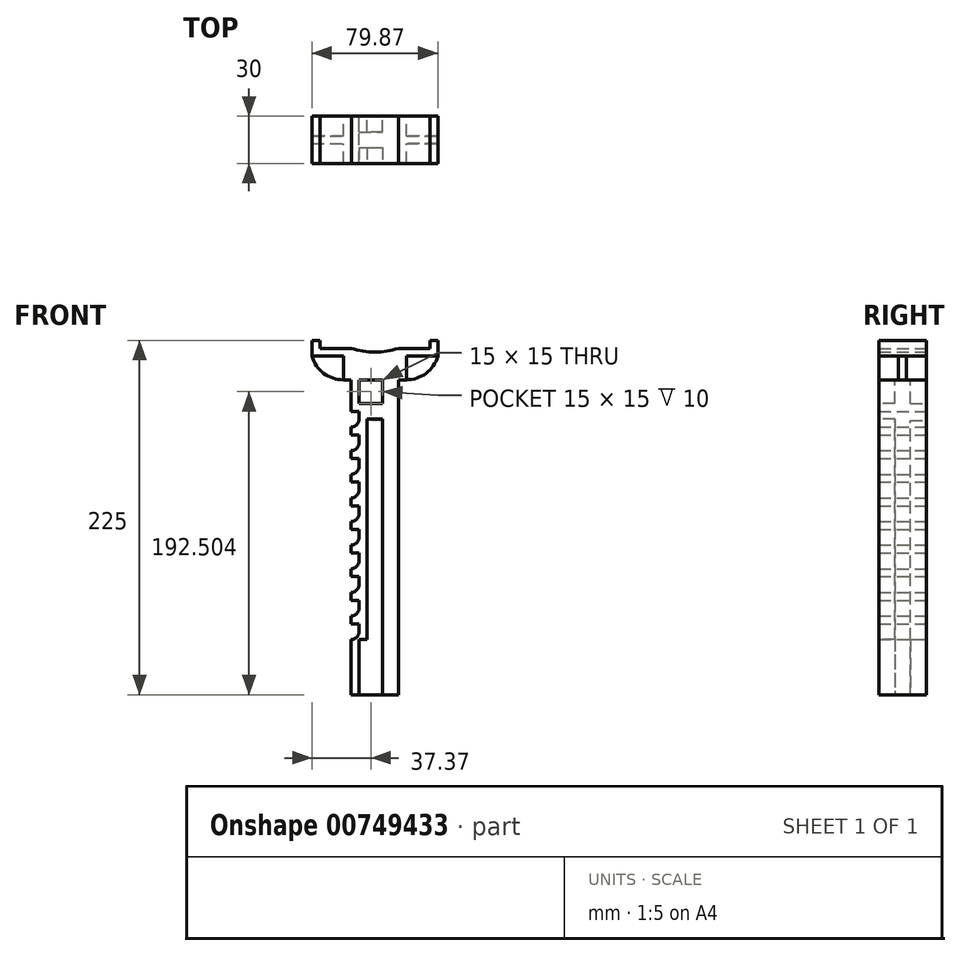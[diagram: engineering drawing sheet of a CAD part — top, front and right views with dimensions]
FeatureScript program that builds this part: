
annotation { "Feature Type Name" : "Feature", "Feature Type Description" : "" }
export const myFeature = defineFeature(function(context is Context, id is Id, definition is map)
    precondition{}
    {
        {
            var Q0;
            Q0=qCreatedBy(makeId("Front.planeOp"),FACE);
            var sketch = newSketch(context, id + "F0", { "sketchPlane" : qUnion([Q0])});
            skLineSegment(sketch, "E0.top", {"start": v(-25, -77.98) * mm, "end": v(5, -77.98) * mm});
            skLineSegment(sketch, "E0.left", {"start": v(-25, 122.02) * mm, "end": v(-25, 102.02) * mm});
            skLineSegment(sketch, "E0.right", {"start": v(5, 122.02) * mm, "end": v(5, -77.98) * mm});
            skLineSegment(sketch, "E1.bottom", {"start": v(-30, 122.02) * mm, "end": v(-25, 122.02) * mm});
            skLineSegment(sketch, "E1.top", {"start": v(-30, 137.02) * mm, "end": v(10, 137.02) * mm});
            skLineSegment(sketch, "E1.left", {"start": v(-30, 122.02) * mm, "end": v(-30, 137.02) * mm});
            skLineSegment(sketch, "E1.right", {"start": v(10, 122.02) * mm, "end": v(10, 137.02) * mm});
            skLineSegment(sketch, "E2", {"start": v(-20, -42.98) * mm, "end": v(-20, -32.98) * mm});
            skPoint(sketch, "E3.start.orphan", {"position": v(-25, 102.02) * mm});
            skPoint(sketch, "E4.start.orphan", {"position": v(-25, -42.98) * mm});
            skLineSegment(sketch, "E5.trimOffspring", {"start": v(-25, -42.98) * mm, "end": v(-25, -77.98) * mm});
            skLineSegment(sketch, "E6", {"start": v(-25, -42.98) * mm, "end": v(-20, -42.98) * mm});
            skLineSegment(sketch, "E7", {"start": v(-25, 102.02) * mm, "end": v(-20, 102.02) * mm});
            skPoint(sketch, "E8.orphan", {"position": v(-20, -77.98) * mm});
            skLineSegment(sketch, "E9.trimOffspring", {"start": v(5, 122.02) * mm, "end": v(10, 122.02) * mm});
            skLineSegment(sketch, "E10.bottom", {"start": v(-20, 92.02) * mm, "end": v(-25, 92.02) * mm});
            skLineSegment(sketch, "E10.top", {"start": v(-20, 87.02) * mm, "end": v(-25, 87.02) * mm});
            skLineSegment(sketch, "E10.right", {"start": v(-25, 92.02) * mm, "end": v(-25, 87.02) * mm});
            skLineSegment(sketch, "E11.bottom", {"start": v(-20, 77.02) * mm, "end": v(-25, 77.02) * mm});
            skLineSegment(sketch, "E11.top", {"start": v(-20, 72.02) * mm, "end": v(-25, 72.02) * mm});
            skLineSegment(sketch, "E11.right", {"start": v(-25, 77.02) * mm, "end": v(-25, 72.02) * mm});
            skLineSegment(sketch, "E12.bottom", {"start": v(-20, 62.02) * mm, "end": v(-25, 62.02) * mm});
            skLineSegment(sketch, "E12.top", {"start": v(-20, 57.02) * mm, "end": v(-25, 57.02) * mm});
            skLineSegment(sketch, "E12.right", {"start": v(-25, 62.02) * mm, "end": v(-25, 57.02) * mm});
            skLineSegment(sketch, "E13.bottom", {"start": v(-20, 47.02) * mm, "end": v(-25, 47.02) * mm});
            skLineSegment(sketch, "E13.top", {"start": v(-20, 42.02) * mm, "end": v(-25, 42.02) * mm});
            skLineSegment(sketch, "E13.right", {"start": v(-25, 47.02) * mm, "end": v(-25, 42.02) * mm});
            skLineSegment(sketch, "E14.bottom", {"start": v(-20, 32.02) * mm, "end": v(-25, 32.02) * mm});
            skLineSegment(sketch, "E14.top", {"start": v(-20, 27.02) * mm, "end": v(-25, 27.02) * mm});
            skLineSegment(sketch, "E14.right", {"start": v(-25, 32.02) * mm, "end": v(-25, 27.02) * mm});
            skLineSegment(sketch, "E15.bottom", {"start": v(-20, 17.02) * mm, "end": v(-25, 17.02) * mm});
            skLineSegment(sketch, "E15.top", {"start": v(-20, 12.02) * mm, "end": v(-25, 12.02) * mm});
            skLineSegment(sketch, "E15.right", {"start": v(-25, 17.02) * mm, "end": v(-25, 12.02) * mm});
            skLineSegment(sketch, "E16.bottom", {"start": v(-20, 2.02) * mm, "end": v(-25, 2.02) * mm});
            skLineSegment(sketch, "E16.top", {"start": v(-20, -2.98) * mm, "end": v(-25, -2.98) * mm});
            skLineSegment(sketch, "E16.right", {"start": v(-25, 2.02) * mm, "end": v(-25, -2.98) * mm});
            skLineSegment(sketch, "E17.bottom", {"start": v(-20, -12.98) * mm, "end": v(-25, -12.98) * mm});
            skLineSegment(sketch, "E17.top", {"start": v(-20, -17.98) * mm, "end": v(-25, -17.98) * mm});
            skLineSegment(sketch, "E17.right", {"start": v(-25, -12.98) * mm, "end": v(-25, -17.98) * mm});
            skLineSegment(sketch, "E18.bottom", {"start": v(-20, -27.98) * mm, "end": v(-25, -27.98) * mm});
            skLineSegment(sketch, "E18.top", {"start": v(-20, -32.98) * mm, "end": v(-25, -32.98) * mm});
            skLineSegment(sketch, "E18.right", {"start": v(-25, -27.98) * mm, "end": v(-25, -32.98) * mm});
            skLineSegment(sketch, "E19.trimOffspring", {"start": v(-20, 92.02) * mm, "end": v(-20, 102.02) * mm});
            skLineSegment(sketch, "E20.trimOffspring", {"start": v(-20, 77.02) * mm, "end": v(-20, 87.02) * mm});
            skLineSegment(sketch, "E21.trimOffspring", {"start": v(-20, 62.02) * mm, "end": v(-20, 72.02) * mm});
            skLineSegment(sketch, "E22.trimOffspring", {"start": v(-20, 47.02) * mm, "end": v(-20, 57.02) * mm});
            skLineSegment(sketch, "E23.trimOffspring", {"start": v(-20, 32.02) * mm, "end": v(-20, 42.02) * mm});
            skLineSegment(sketch, "E24.trimOffspring", {"start": v(-20, 17.02) * mm, "end": v(-20, 27.02) * mm});
            skLineSegment(sketch, "E25.trimOffspring", {"start": v(-20, 2.02) * mm, "end": v(-20, 12.02) * mm});
            skLineSegment(sketch, "E26.trimOffspring", {"start": v(-20, -12.98) * mm, "end": v(-20, -2.98) * mm});
            skLineSegment(sketch, "E27.trimOffspring", {"start": v(-20, -27.98) * mm, "end": v(-20, -17.98) * mm});
            skSolve(sketch);
        }
        {
            var Q0;
            Q0 = qSketchRegion(id + "F0", true);
            extrude(context, id + "F1", {"entities" : qUnion([Q0]), "depth" : 30 * mm, "offsetDistance" : 25 * mm});
        }
        {
            var Q0;
            Q0=makeQuery(id+"F1.opExtrude","SWEPT_EDGE",EDGE,{"disambiguationData":[OSD([sQuery(id+"F0.wireOp",EDGE,"E10.bottom"),sQuery(id+"F0.wireOp",EDGE,"E19.trimOffspring")])]});
            var Q1;
            Q1=makeQuery(id+"F1.opExtrude","SWEPT_EDGE",EDGE,{"disambiguationData":[OSD([sQuery(id+"F0.wireOp",EDGE,"E11.bottom"),sQuery(id+"F0.wireOp",EDGE,"E20.trimOffspring")])]});
            var Q2;
            Q2=makeQuery(id+"F1.opExtrude","SWEPT_EDGE",EDGE,{"disambiguationData":[OSD([sQuery(id+"F0.wireOp",EDGE,"E12.bottom"),sQuery(id+"F0.wireOp",EDGE,"E21.trimOffspring")])]});
            var Q3;
            Q3=makeQuery(id+"F1.opExtrude","SWEPT_EDGE",EDGE,{"disambiguationData":[OSD([sQuery(id+"F0.wireOp",EDGE,"E13.bottom"),sQuery(id+"F0.wireOp",EDGE,"E22.trimOffspring")])]});
            var Q4;
            Q4=makeQuery(id+"F1.opExtrude","SWEPT_EDGE",EDGE,{"disambiguationData":[OSD([sQuery(id+"F0.wireOp",EDGE,"E14.bottom"),sQuery(id+"F0.wireOp",EDGE,"E23.trimOffspring")])]});
            var Q5;
            Q5=makeQuery(id+"F1.opExtrude","SWEPT_EDGE",EDGE,{"disambiguationData":[OSD([sQuery(id+"F0.wireOp",EDGE,"E15.bottom"),sQuery(id+"F0.wireOp",EDGE,"E24.trimOffspring")])]});
            var Q6;
            Q6=makeQuery(id+"F1.opExtrude","SWEPT_EDGE",EDGE,{"disambiguationData":[OSD([sQuery(id+"F0.wireOp",EDGE,"E16.bottom"),sQuery(id+"F0.wireOp",EDGE,"E25.trimOffspring")])]});
            var Q7;
            Q7=makeQuery(id+"F1.opExtrude","SWEPT_EDGE",EDGE,{"disambiguationData":[OSD([sQuery(id+"F0.wireOp",EDGE,"E17.bottom"),sQuery(id+"F0.wireOp",EDGE,"E26.trimOffspring")])]});
            var Q8;
            Q8=makeQuery(id+"F1.opExtrude","SWEPT_EDGE",EDGE,{"disambiguationData":[OSD([sQuery(id+"F0.wireOp",EDGE,"E18.bottom"),sQuery(id+"F0.wireOp",EDGE,"E27.trimOffspring")])]});
            var Q9;
            Q9=makeQuery(id+"F1.opExtrude","SWEPT_EDGE",EDGE,{"disambiguationData":[OSD([sQuery(id+"F0.wireOp",EDGE,"E2"),sQuery(id+"F0.wireOp",EDGE,"E6")])]});
            fillet(context, id + "F2", {"entities" : qUnion([Q0, Q1, Q2, Q3, Q4, Q5, Q6, Q7, Q8, Q9]), "radius" : 5 * mm, "tangentPropagation" : true, "allowEdgeOverflow" : false});
        }
        {
            var Q0;
            Q0=makeQuery(id+"F1.opExtrude","CAP_FACE",FACE,{"disambiguationData":[OSD([sQuery(id+"F0.wireOp",EDGE,"E0.top"),sQuery(id+"F0.wireOp",EDGE,"E0.left"),sQuery(id+"F0.wireOp",EDGE,"E0.right"),sQuery(id+"F0.wireOp",EDGE,"E1.bottom"),sQuery(id+"F0.wireOp",EDGE,"E1.top"),sQuery(id+"F0.wireOp",EDGE,"E1.left"),sQuery(id+"F0.wireOp",EDGE,"E1.right"),sQuery(id+"F0.wireOp",EDGE,"E2"),sQuery(id+"F0.wireOp",EDGE,"E5.trimOffspring"),sQuery(id+"F0.wireOp",EDGE,"E6"),sQuery(id+"F0.wireOp",EDGE,"E7"),sQuery(id+"F0.wireOp",EDGE,"E9.trimOffspring"),sQuery(id+"F0.wireOp",EDGE,"E10.bottom"),sQuery(id+"F0.wireOp",EDGE,"E10.top"),sQuery(id+"F0.wireOp",EDGE,"E10.right"),sQuery(id+"F0.wireOp",EDGE,"E11.bottom"),sQuery(id+"F0.wireOp",EDGE,"E11.top"),sQuery(id+"F0.wireOp",EDGE,"E11.right"),sQuery(id+"F0.wireOp",EDGE,"E12.bottom"),sQuery(id+"F0.wireOp",EDGE,"E12.top"),sQuery(id+"F0.wireOp",EDGE,"E12.right"),sQuery(id+"F0.wireOp",EDGE,"E13.bottom"),sQuery(id+"F0.wireOp",EDGE,"E13.top"),sQuery(id+"F0.wireOp",EDGE,"E13.right"),sQuery(id+"F0.wireOp",EDGE,"E14.bottom"),sQuery(id+"F0.wireOp",EDGE,"E14.top"),sQuery(id+"F0.wireOp",EDGE,"E14.right"),sQuery(id+"F0.wireOp",EDGE,"E15.bottom"),sQuery(id+"F0.wireOp",EDGE,"E15.top"),sQuery(id+"F0.wireOp",EDGE,"E15.right"),sQuery(id+"F0.wireOp",EDGE,"E16.bottom"),sQuery(id+"F0.wireOp",EDGE,"E16.top"),sQuery(id+"F0.wireOp",EDGE,"E16.right"),sQuery(id+"F0.wireOp",EDGE,"E17.bottom"),sQuery(id+"F0.wireOp",EDGE,"E17.top"),sQuery(id+"F0.wireOp",EDGE,"E17.right"),sQuery(id+"F0.wireOp",EDGE,"E18.bottom"),sQuery(id+"F0.wireOp",EDGE,"E18.top"),sQuery(id+"F0.wireOp",EDGE,"E18.right"),sQuery(id+"F0.wireOp",EDGE,"E19.trimOffspring"),sQuery(id+"F0.wireOp",EDGE,"E20.trimOffspring"),sQuery(id+"F0.wireOp",EDGE,"E21.trimOffspring"),sQuery(id+"F0.wireOp",EDGE,"E22.trimOffspring"),sQuery(id+"F0.wireOp",EDGE,"E23.trimOffspring"),sQuery(id+"F0.wireOp",EDGE,"E24.trimOffspring"),sQuery(id+"F0.wireOp",EDGE,"E25.trimOffspring"),sQuery(id+"F0.wireOp",EDGE,"E26.trimOffspring"),sQuery(id+"F0.wireOp",EDGE,"E27.trimOffspring")])],"isStart":false});
            var sketch = newSketch(context, id + "F3", { "sketchPlane" : qUnion([Q0])});
            skLineSegment(sketch, "E28", {"start": v(-20, -42.98) * mm, "end": v(-20, -77.98) * mm});
            skLineSegment(sketch, "E29", {"start": v(-20, -42.98) * mm, "end": v(-15, -42.98) * mm});
            skLineSegment(sketch, "E30", {"start": v(-15, -42.98) * mm, "end": v(-15, 97.02) * mm});
            skLineSegment(sketch, "E31", {"start": v(-15, 97.02) * mm, "end": v(-5, 97.02) * mm});
            skLineSegment(sketch, "E32", {"start": v(-20, 107.02) * mm, "end": v(-5, 107.02) * mm});
            skLineSegment(sketch, "E33", {"start": v(-5, 122.02) * mm, "end": v(-5, 107.02) * mm});
            skLineSegment(sketch, "E34.trimOffspring", {"start": v(-5, 97.02) * mm, "end": v(-5, -77.98) * mm});
            skPoint(sketch, "E35.orphan", {"position": v(-20, 97.02) * mm});
            skLineSegment(sketch, "E36", {"start": v(-20, 107.02) * mm, "end": v(-20, 122.02) * mm});
            skLineSegment(sketch, "E37", {"start": v(-20, 122.02) * mm, "end": v(-5, 122.02) * mm});
            skPoint(sketch, "E38.orphan", {"position": v(-25, 107.02) * mm});
            skLineSegment(sketch, "E39.0.0", {"start": v(-20, 57.02) * mm, "end": v(-20, 52.02) * mm});
            skArc(sketch, "E39.0.1", {"start": v(-20, 52.02) * mm, "mid": v(-21.46, 48.49) * mm, "end": v(-25, 47.02) * mm});
            skLineSegment(sketch, "E39.0.2", {"start": v(-25, 47.02) * mm, "end": v(-25, 42.02) * mm});
            skLineSegment(sketch, "E39.0.3", {"start": v(-25, 42.02) * mm, "end": v(-20, 42.02) * mm});
            skLineSegment(sketch, "E39.0.4", {"start": v(-20, 42.02) * mm, "end": v(-20, 37.02) * mm});
            skArc(sketch, "E39.0.5", {"start": v(-20, 37.02) * mm, "mid": v(-21.46, 33.49) * mm, "end": v(-25, 32.02) * mm});
            skLineSegment(sketch, "E39.0.6", {"start": v(-25, 32.02) * mm, "end": v(-25, 27.02) * mm});
            skLineSegment(sketch, "E39.0.7", {"start": v(-25, 27.02) * mm, "end": v(-20, 27.02) * mm});
            skLineSegment(sketch, "E39.0.8", {"start": v(-20, 27.02) * mm, "end": v(-20, 22.02) * mm});
            skArc(sketch, "E39.0.9", {"start": v(-20, 22.02) * mm, "mid": v(-21.46, 18.49) * mm, "end": v(-25, 17.02) * mm});
            skLineSegment(sketch, "E39.0.10", {"start": v(-25, 17.02) * mm, "end": v(-25, 12.02) * mm});
            skLineSegment(sketch, "E39.0.11", {"start": v(-25, 12.02) * mm, "end": v(-20, 12.02) * mm});
            skLineSegment(sketch, "E39.0.12", {"start": v(-20, 12.02) * mm, "end": v(-20, 7.02) * mm});
            skArc(sketch, "E39.0.13", {"start": v(-20, 7.02) * mm, "mid": v(-21.46, 3.49) * mm, "end": v(-25, 2.02) * mm});
            skLineSegment(sketch, "E39.0.14", {"start": v(-25, 2.02) * mm, "end": v(-25, -2.98) * mm});
            skLineSegment(sketch, "E39.0.15", {"start": v(-25, -2.98) * mm, "end": v(-20, -2.98) * mm});
            skLineSegment(sketch, "E39.0.16", {"start": v(-20, -2.98) * mm, "end": v(-20, -7.98) * mm});
            skArc(sketch, "E39.0.17", {"start": v(-20, -7.98) * mm, "mid": v(-21.46, -11.51) * mm, "end": v(-25, -12.98) * mm});
            skLineSegment(sketch, "E39.0.18", {"start": v(-25, -12.98) * mm, "end": v(-25, -17.98) * mm});
            skLineSegment(sketch, "E39.0.19", {"start": v(-25, -17.98) * mm, "end": v(-20, -17.98) * mm});
            skLineSegment(sketch, "E39.0.20", {"start": v(-20, -17.98) * mm, "end": v(-20, -22.98) * mm});
            skArc(sketch, "E39.0.21", {"start": v(-20, -22.98) * mm, "mid": v(-21.46, -26.51) * mm, "end": v(-25, -27.98) * mm});
            skLineSegment(sketch, "E39.0.22", {"start": v(-25, -27.98) * mm, "end": v(-25, -32.98) * mm});
            skLineSegment(sketch, "E39.0.23", {"start": v(-25, -32.98) * mm, "end": v(-20, -32.98) * mm});
            skLineSegment(sketch, "E39.0.24", {"start": v(-20, -32.98) * mm, "end": v(-20, -37.98) * mm});
            skArc(sketch, "E39.0.25", {"start": v(-20, -37.98) * mm, "mid": v(-21.46, -41.51) * mm, "end": v(-25, -42.98) * mm});
            skLineSegment(sketch, "E39.0.26", {"start": v(-25, -42.98) * mm, "end": v(-25, -77.98) * mm});
            skLineSegment(sketch, "E39.0.27", {"start": v(-25, -77.98) * mm, "end": v(5, -77.98) * mm});
            skLineSegment(sketch, "E39.0.28", {"start": v(5, -77.98) * mm, "end": v(5, 122.02) * mm});
            skLineSegment(sketch, "E39.0.29", {"start": v(5, 122.02) * mm, "end": v(10, 122.02) * mm});
            skLineSegment(sketch, "E39.0.30", {"start": v(10, 122.02) * mm, "end": v(10, 137.02) * mm});
            skLineSegment(sketch, "E39.0.31", {"start": v(10, 137.02) * mm, "end": v(-30, 137.02) * mm});
            skLineSegment(sketch, "E39.0.32", {"start": v(-30, 137.02) * mm, "end": v(-30, 122.02) * mm});
            skLineSegment(sketch, "E39.0.33", {"start": v(-30, 122.02) * mm, "end": v(-25, 122.02) * mm});
            skLineSegment(sketch, "E39.0.34", {"start": v(-25, 122.02) * mm, "end": v(-25, 102.02) * mm});
            skLineSegment(sketch, "E39.0.35", {"start": v(-25, 102.02) * mm, "end": v(-20, 102.02) * mm});
            skLineSegment(sketch, "E39.0.36", {"start": v(-20, 102.02) * mm, "end": v(-20, 97.02) * mm});
            skArc(sketch, "E39.0.37", {"start": v(-20, 97.02) * mm, "mid": v(-21.46, 93.49) * mm, "end": v(-25, 92.02) * mm});
            skLineSegment(sketch, "E39.0.38", {"start": v(-25, 92.02) * mm, "end": v(-25, 87.02) * mm});
            skLineSegment(sketch, "E39.0.39", {"start": v(-25, 87.02) * mm, "end": v(-20, 87.02) * mm});
            skLineSegment(sketch, "E39.0.40", {"start": v(-20, 87.02) * mm, "end": v(-20, 82.02) * mm});
            skArc(sketch, "E39.0.41", {"start": v(-20, 82.02) * mm, "mid": v(-21.46, 78.49) * mm, "end": v(-25, 77.02) * mm});
            skLineSegment(sketch, "E39.0.42", {"start": v(-25, 77.02) * mm, "end": v(-25, 72.02) * mm});
            skLineSegment(sketch, "E39.0.43", {"start": v(-25, 72.02) * mm, "end": v(-20, 72.02) * mm});
            skLineSegment(sketch, "E39.0.44", {"start": v(-20, 72.02) * mm, "end": v(-20, 67.02) * mm});
            skArc(sketch, "E39.0.45", {"start": v(-20, 67.02) * mm, "mid": v(-21.46, 63.49) * mm, "end": v(-25, 62.02) * mm});
            skLineSegment(sketch, "E39.0.46", {"start": v(-25, 62.02) * mm, "end": v(-25, 57.02) * mm});
            skLineSegment(sketch, "E39.0.47", {"start": v(-25, 57.02) * mm, "end": v(-20, 57.02) * mm});
            skSolve(sketch);
        }
        {
            var Q0;
            {var subQ0=sQuery(id+"F3.wireOp",EDGE,"E28");Q0=makeQuery(id+"F3.imprint","IMPRINT",FACE,{"disambiguationData":[TD([[makeQuery(id+"F3.imprint","IMPRINT",EDGE,{"derivedFrom":subQ0}),1.0]])]});}
            var Q1;
            Q1=makeQuery(id+"F3.imprint","IMPRINT",FACE,{"disambiguationData":[TD([[makeQuery(id+"F3.imprint","IMPRINT",EDGE,{"derivedFrom":sQuery(id+"F3.wireOp",EDGE,"E32")}),1.0]])]});
            extrude(context, id + "F4", {"entities" : qUnion([Q0, Q1]), "operationType" : NewBodyOperationType.REMOVE, "oppositeDirection" : true, "depth" : 10 * mm, "offsetDistance" : 25 * mm});
        }
        {
            var Q0;
            Q0=makeQuery(id+"F1.opExtrude","CAP_FACE",FACE,{"disambiguationData":[OSD([sQuery(id+"F0.wireOp",EDGE,"E0.top"),sQuery(id+"F0.wireOp",EDGE,"E0.left"),sQuery(id+"F0.wireOp",EDGE,"E0.right"),sQuery(id+"F0.wireOp",EDGE,"E1.bottom"),sQuery(id+"F0.wireOp",EDGE,"E1.top"),sQuery(id+"F0.wireOp",EDGE,"E1.left"),sQuery(id+"F0.wireOp",EDGE,"E1.right"),sQuery(id+"F0.wireOp",EDGE,"E2"),sQuery(id+"F0.wireOp",EDGE,"E5.trimOffspring"),sQuery(id+"F0.wireOp",EDGE,"E6"),sQuery(id+"F0.wireOp",EDGE,"E7"),sQuery(id+"F0.wireOp",EDGE,"E9.trimOffspring"),sQuery(id+"F0.wireOp",EDGE,"E10.bottom"),sQuery(id+"F0.wireOp",EDGE,"E10.top"),sQuery(id+"F0.wireOp",EDGE,"E10.right"),sQuery(id+"F0.wireOp",EDGE,"E11.bottom"),sQuery(id+"F0.wireOp",EDGE,"E11.top"),sQuery(id+"F0.wireOp",EDGE,"E11.right"),sQuery(id+"F0.wireOp",EDGE,"E12.bottom"),sQuery(id+"F0.wireOp",EDGE,"E12.top"),sQuery(id+"F0.wireOp",EDGE,"E12.right"),sQuery(id+"F0.wireOp",EDGE,"E13.bottom"),sQuery(id+"F0.wireOp",EDGE,"E13.top"),sQuery(id+"F0.wireOp",EDGE,"E13.right"),sQuery(id+"F0.wireOp",EDGE,"E14.bottom"),sQuery(id+"F0.wireOp",EDGE,"E14.top"),sQuery(id+"F0.wireOp",EDGE,"E14.right"),sQuery(id+"F0.wireOp",EDGE,"E15.bottom"),sQuery(id+"F0.wireOp",EDGE,"E15.top"),sQuery(id+"F0.wireOp",EDGE,"E15.right"),sQuery(id+"F0.wireOp",EDGE,"E16.bottom"),sQuery(id+"F0.wireOp",EDGE,"E16.top"),sQuery(id+"F0.wireOp",EDGE,"E16.right"),sQuery(id+"F0.wireOp",EDGE,"E17.bottom"),sQuery(id+"F0.wireOp",EDGE,"E17.top"),sQuery(id+"F0.wireOp",EDGE,"E17.right"),sQuery(id+"F0.wireOp",EDGE,"E18.bottom"),sQuery(id+"F0.wireOp",EDGE,"E18.top"),sQuery(id+"F0.wireOp",EDGE,"E18.right"),sQuery(id+"F0.wireOp",EDGE,"E19.trimOffspring"),sQuery(id+"F0.wireOp",EDGE,"E20.trimOffspring"),sQuery(id+"F0.wireOp",EDGE,"E21.trimOffspring"),sQuery(id+"F0.wireOp",EDGE,"E22.trimOffspring"),sQuery(id+"F0.wireOp",EDGE,"E23.trimOffspring"),sQuery(id+"F0.wireOp",EDGE,"E24.trimOffspring"),sQuery(id+"F0.wireOp",EDGE,"E25.trimOffspring"),sQuery(id+"F0.wireOp",EDGE,"E26.trimOffspring"),sQuery(id+"F0.wireOp",EDGE,"E27.trimOffspring")])],"isStart":true});
            var sketch = newSketch(context, id + "F5", { "sketchPlane" : qUnion([Q0])});
            skLineSegment(sketch, "E40", {"start": v(20, -42.98) * mm, "end": v(20, -77.98) * mm});
            skLineSegment(sketch, "E41", {"start": v(20, -42.98) * mm, "end": v(15, -42.98) * mm});
            skLineSegment(sketch, "E42", {"start": v(15, -42.98) * mm, "end": v(15, 96.1) * mm});
            skLineSegment(sketch, "E43", {"start": v(5, -77.98) * mm, "end": v(5, 96.1) * mm});
            skLineSegment(sketch, "E44", {"start": v(5, 96.1) * mm, "end": v(15, 96.1) * mm});
            skLineSegment(sketch, "E45", {"start": v(5, 122.02) * mm, "end": v(20, 122.02) * mm});
            skLineSegment(sketch, "E46", {"start": v(20, 122.02) * mm, "end": v(20, 107.02) * mm});
            skLineSegment(sketch, "E47", {"start": v(5, 107.02) * mm, "end": v(20, 107.02) * mm});
            skLineSegment(sketch, "E48", {"start": v(5, 107.02) * mm, "end": v(5, 122.02) * mm});
            skSolve(sketch);
        }
        {
            var Q0;
            {var subQ1=sQuery(id+"F5.wireOp",EDGE,"E40");Q0=makeQuery(id+"F5.imprint","IMPRINT",FACE,{"disambiguationData":[TD([[makeQuery(id+"F5.imprint","IMPRINT",EDGE,{"derivedFrom":subQ1}),-1.0]])]});}
            var Q1;
            Q1=makeQuery(id+"F5.imprint","IMPRINT",FACE,{"disambiguationData":[TD([[makeQuery(id+"F5.imprint","IMPRINT",EDGE,{"derivedFrom":sQuery(id+"F5.wireOp",EDGE,"E45")}),-1.0]])]});
            extrude(context, id + "F6", {"entities" : qUnion([Q0, Q1]), "operationType" : NewBodyOperationType.REMOVE, "oppositeDirection" : true, "depth" : 10 * mm, "offsetDistance" : 25 * mm});
        }
        {
            var Q0;
            Q0=makeQuery(id+"F1.opExtrude","CAP_FACE",FACE,{"disambiguationData":[OSD([sQuery(id+"F0.wireOp",EDGE,"E0.top"),sQuery(id+"F0.wireOp",EDGE,"E0.left"),sQuery(id+"F0.wireOp",EDGE,"E0.right"),sQuery(id+"F0.wireOp",EDGE,"E1.bottom"),sQuery(id+"F0.wireOp",EDGE,"E1.top"),sQuery(id+"F0.wireOp",EDGE,"E1.left"),sQuery(id+"F0.wireOp",EDGE,"E1.right"),sQuery(id+"F0.wireOp",EDGE,"E2"),sQuery(id+"F0.wireOp",EDGE,"E5.trimOffspring"),sQuery(id+"F0.wireOp",EDGE,"E6"),sQuery(id+"F0.wireOp",EDGE,"E7"),sQuery(id+"F0.wireOp",EDGE,"E9.trimOffspring"),sQuery(id+"F0.wireOp",EDGE,"E10.bottom"),sQuery(id+"F0.wireOp",EDGE,"E10.top"),sQuery(id+"F0.wireOp",EDGE,"E10.right"),sQuery(id+"F0.wireOp",EDGE,"E11.bottom"),sQuery(id+"F0.wireOp",EDGE,"E11.top"),sQuery(id+"F0.wireOp",EDGE,"E11.right"),sQuery(id+"F0.wireOp",EDGE,"E12.bottom"),sQuery(id+"F0.wireOp",EDGE,"E12.top"),sQuery(id+"F0.wireOp",EDGE,"E12.right"),sQuery(id+"F0.wireOp",EDGE,"E13.bottom"),sQuery(id+"F0.wireOp",EDGE,"E13.top"),sQuery(id+"F0.wireOp",EDGE,"E13.right"),sQuery(id+"F0.wireOp",EDGE,"E14.bottom"),sQuery(id+"F0.wireOp",EDGE,"E14.top"),sQuery(id+"F0.wireOp",EDGE,"E14.right"),sQuery(id+"F0.wireOp",EDGE,"E15.bottom"),sQuery(id+"F0.wireOp",EDGE,"E15.top"),sQuery(id+"F0.wireOp",EDGE,"E15.right"),sQuery(id+"F0.wireOp",EDGE,"E16.bottom"),sQuery(id+"F0.wireOp",EDGE,"E16.top"),sQuery(id+"F0.wireOp",EDGE,"E16.right"),sQuery(id+"F0.wireOp",EDGE,"E17.bottom"),sQuery(id+"F0.wireOp",EDGE,"E17.top"),sQuery(id+"F0.wireOp",EDGE,"E17.right"),sQuery(id+"F0.wireOp",EDGE,"E18.bottom"),sQuery(id+"F0.wireOp",EDGE,"E18.top"),sQuery(id+"F0.wireOp",EDGE,"E18.right"),sQuery(id+"F0.wireOp",EDGE,"E19.trimOffspring"),sQuery(id+"F0.wireOp",EDGE,"E20.trimOffspring"),sQuery(id+"F0.wireOp",EDGE,"E21.trimOffspring"),sQuery(id+"F0.wireOp",EDGE,"E22.trimOffspring"),sQuery(id+"F0.wireOp",EDGE,"E23.trimOffspring"),sQuery(id+"F0.wireOp",EDGE,"E24.trimOffspring"),sQuery(id+"F0.wireOp",EDGE,"E25.trimOffspring"),sQuery(id+"F0.wireOp",EDGE,"E26.trimOffspring"),sQuery(id+"F0.wireOp",EDGE,"E27.trimOffspring")])],"isStart":true});
            var sketch = newSketch(context, id + "F7", { "sketchPlane" : qUnion([Q0])});
            skLineSegment(sketch, "E49.bottom", {"start": v(-30, 137.02) * mm, "end": v(49.87, 137.02) * mm});
            skLineSegment(sketch, "E49.top", {"start": v(-25, 142.02) * mm, "end": v(44.87, 142.02) * mm});
            skLineSegment(sketch, "E50.top", {"start": v(-30, 147.02) * mm, "end": v(-25, 147.02) * mm});
            skLineSegment(sketch, "E50.right", {"start": v(-25, 142.02) * mm, "end": v(-25, 147.02) * mm});
            skLineSegment(sketch, "E51.top", {"start": v(49.87, 147.02) * mm, "end": v(44.87, 147.02) * mm});
            skLineSegment(sketch, "E51.right", {"start": v(44.87, 142.02) * mm, "end": v(44.87, 147.02) * mm});
            skLineSegment(sketch, "E52", {"start": v(-30, 147.02) * mm, "end": v(-30, 137.02) * mm});
            skLineSegment(sketch, "E53", {"start": v(49.87, 137.02) * mm, "end": v(49.87, 147.02) * mm});
            skSolve(sketch);
        }
        {
            var Q0;
            Q0 = qSketchRegion(id + "F7", true);
            extrude(context, id + "F8", {"entities" : qUnion([Q0]), "operationType" : NewBodyOperationType.ADD, "depth" : -30 * mm, "offsetDistance" : 25 * mm});
        }
        {
            var Q0;
            Q0=makeQuery(id+"F8.boolean.opBoolean","MERGE",FACE,{"derivedFrom":[makeQuery(id+"F1.opExtrude","CAP_FACE",FACE,{"disambiguationData":[OSD([sQuery(id+"F0.wireOp",EDGE,"E0.top"),sQuery(id+"F0.wireOp",EDGE,"E0.left"),sQuery(id+"F0.wireOp",EDGE,"E0.right"),sQuery(id+"F0.wireOp",EDGE,"E1.bottom"),sQuery(id+"F0.wireOp",EDGE,"E1.top"),sQuery(id+"F0.wireOp",EDGE,"E1.left"),sQuery(id+"F0.wireOp",EDGE,"E1.right"),sQuery(id+"F0.wireOp",EDGE,"E2"),sQuery(id+"F0.wireOp",EDGE,"E5.trimOffspring"),sQuery(id+"F0.wireOp",EDGE,"E6"),sQuery(id+"F0.wireOp",EDGE,"E7"),sQuery(id+"F0.wireOp",EDGE,"E9.trimOffspring"),sQuery(id+"F0.wireOp",EDGE,"E10.bottom"),sQuery(id+"F0.wireOp",EDGE,"E10.top"),sQuery(id+"F0.wireOp",EDGE,"E10.right"),sQuery(id+"F0.wireOp",EDGE,"E11.bottom"),sQuery(id+"F0.wireOp",EDGE,"E11.top"),sQuery(id+"F0.wireOp",EDGE,"E11.right"),sQuery(id+"F0.wireOp",EDGE,"E12.bottom"),sQuery(id+"F0.wireOp",EDGE,"E12.top"),sQuery(id+"F0.wireOp",EDGE,"E12.right"),sQuery(id+"F0.wireOp",EDGE,"E13.bottom"),sQuery(id+"F0.wireOp",EDGE,"E13.top"),sQuery(id+"F0.wireOp",EDGE,"E13.right"),sQuery(id+"F0.wireOp",EDGE,"E14.bottom"),sQuery(id+"F0.wireOp",EDGE,"E14.top"),sQuery(id+"F0.wireOp",EDGE,"E14.right"),sQuery(id+"F0.wireOp",EDGE,"E15.bottom"),sQuery(id+"F0.wireOp",EDGE,"E15.top"),sQuery(id+"F0.wireOp",EDGE,"E15.right"),sQuery(id+"F0.wireOp",EDGE,"E16.bottom"),sQuery(id+"F0.wireOp",EDGE,"E16.top"),sQuery(id+"F0.wireOp",EDGE,"E16.right"),sQuery(id+"F0.wireOp",EDGE,"E17.bottom"),sQuery(id+"F0.wireOp",EDGE,"E17.top"),sQuery(id+"F0.wireOp",EDGE,"E17.right"),sQuery(id+"F0.wireOp",EDGE,"E18.bottom"),sQuery(id+"F0.wireOp",EDGE,"E18.top"),sQuery(id+"F0.wireOp",EDGE,"E18.right"),sQuery(id+"F0.wireOp",EDGE,"E19.trimOffspring"),sQuery(id+"F0.wireOp",EDGE,"E20.trimOffspring"),sQuery(id+"F0.wireOp",EDGE,"E21.trimOffspring"),sQuery(id+"F0.wireOp",EDGE,"E22.trimOffspring"),sQuery(id+"F0.wireOp",EDGE,"E23.trimOffspring"),sQuery(id+"F0.wireOp",EDGE,"E24.trimOffspring"),sQuery(id+"F0.wireOp",EDGE,"E25.trimOffspring"),sQuery(id+"F0.wireOp",EDGE,"E26.trimOffspring"),sQuery(id+"F0.wireOp",EDGE,"E27.trimOffspring")])],"isStart":false}),makeQuery(id+"F8.opExtrude","CAP_FACE",FACE,{"disambiguationData":[OSD([sQuery(id+"F7.wireOp",EDGE,"E49.bottom"),sQuery(id+"F7.wireOp",EDGE,"E49.top"),sQuery(id+"F7.wireOp",EDGE,"E50.top"),sQuery(id+"F7.wireOp",EDGE,"E50.right"),sQuery(id+"F7.wireOp",EDGE,"E51.top"),sQuery(id+"F7.wireOp",EDGE,"E51.right"),sQuery(id+"F7.wireOp",EDGE,"E52"),sQuery(id+"F7.wireOp",EDGE,"E53")])],"isStart":false})]});
            var sketch = newSketch(context, id + "F9", { "sketchPlane" : qUnion([Q0])});
            skArc(sketch, "E54", {"start": v(-49.87, 137.02) * mm, "mid": v(-42.45, 126.2) * mm, "end": v(-30, 122.02) * mm});
            skArc(sketch, "E55", {"start": v(10, 122.02) * mm, "mid": v(22.5, 126.2) * mm, "end": v(30, 137.02) * mm});
            skSolve(sketch);
        }
        {
            var Q0;
            Q0=makeQuery(id+"F9.imprint","IMPRINT",FACE,{"disambiguationData":[TD([[makeQuery(id+"F9.imprint","IMPRINT",EDGE,{"derivedFrom":sQuery(id+"F9.wireOp",EDGE,"E54")}),1.0]])]});
            var Q1;
            Q1=makeQuery(id+"F9.imprint","IMPRINT",FACE,{"disambiguationData":[TD([[makeQuery(id+"F9.imprint","IMPRINT",EDGE,{"derivedFrom":sQuery(id+"F9.wireOp",EDGE,"E55")}),1.0]])]});
            extrude(context, id + "F10", {"entities" : qUnion([Q0, Q1]), "operationType" : NewBodyOperationType.ADD, "depth" : -17.5 * mm, "offsetDistance" : 25 * mm});
        }
        {
            var Q0;
            {var subQ0=sQuery(id+"F7.wireOp",EDGE,"E49.bottom");var subQ1=sQuery(id+"F0.wireOp",EDGE,"E1.right");var subQ2=sQuery(id+"F0.wireOp",EDGE,"E1.left");Q0=makeQuery(id+"F10.boolean.opBoolean","MERGE",FACE,{"derivedFrom":[makeQuery(id+"F8.boolean.opBoolean","MERGE",FACE,{"derivedFrom":[makeQuery(id+"F1.opExtrude","CAP_FACE",FACE,{"disambiguationData":[OSD([sQuery(id+"F0.wireOp",EDGE,"E0.top"),sQuery(id+"F0.wireOp",EDGE,"E0.left"),sQuery(id+"F0.wireOp",EDGE,"E0.right"),sQuery(id+"F0.wireOp",EDGE,"E1.bottom"),sQuery(id+"F0.wireOp",EDGE,"E1.top"),subQ2,subQ1,sQuery(id+"F0.wireOp",EDGE,"E2"),sQuery(id+"F0.wireOp",EDGE,"E5.trimOffspring"),sQuery(id+"F0.wireOp",EDGE,"E6"),sQuery(id+"F0.wireOp",EDGE,"E7"),sQuery(id+"F0.wireOp",EDGE,"E9.trimOffspring"),sQuery(id+"F0.wireOp",EDGE,"E10.bottom"),sQuery(id+"F0.wireOp",EDGE,"E10.top"),sQuery(id+"F0.wireOp",EDGE,"E10.right"),sQuery(id+"F0.wireOp",EDGE,"E11.bottom"),sQuery(id+"F0.wireOp",EDGE,"E11.top"),sQuery(id+"F0.wireOp",EDGE,"E11.right"),sQuery(id+"F0.wireOp",EDGE,"E12.bottom"),sQuery(id+"F0.wireOp",EDGE,"E12.top"),sQuery(id+"F0.wireOp",EDGE,"E12.right"),sQuery(id+"F0.wireOp",EDGE,"E13.bottom"),sQuery(id+"F0.wireOp",EDGE,"E13.top"),sQuery(id+"F0.wireOp",EDGE,"E13.right"),sQuery(id+"F0.wireOp",EDGE,"E14.bottom"),sQuery(id+"F0.wireOp",EDGE,"E14.top"),sQuery(id+"F0.wireOp",EDGE,"E14.right"),sQuery(id+"F0.wireOp",EDGE,"E15.bottom"),sQuery(id+"F0.wireOp",EDGE,"E15.top"),sQuery(id+"F0.wireOp",EDGE,"E15.right"),sQuery(id+"F0.wireOp",EDGE,"E16.bottom"),sQuery(id+"F0.wireOp",EDGE,"E16.top"),sQuery(id+"F0.wireOp",EDGE,"E16.right"),sQuery(id+"F0.wireOp",EDGE,"E17.bottom"),sQuery(id+"F0.wireOp",EDGE,"E17.top"),sQuery(id+"F0.wireOp",EDGE,"E17.right"),sQuery(id+"F0.wireOp",EDGE,"E18.bottom"),sQuery(id+"F0.wireOp",EDGE,"E18.top"),sQuery(id+"F0.wireOp",EDGE,"E18.right"),sQuery(id+"F0.wireOp",EDGE,"E19.trimOffspring"),sQuery(id+"F0.wireOp",EDGE,"E20.trimOffspring"),sQuery(id+"F0.wireOp",EDGE,"E21.trimOffspring"),sQuery(id+"F0.wireOp",EDGE,"E22.trimOffspring"),sQuery(id+"F0.wireOp",EDGE,"E23.trimOffspring"),sQuery(id+"F0.wireOp",EDGE,"E24.trimOffspring"),sQuery(id+"F0.wireOp",EDGE,"E25.trimOffspring"),sQuery(id+"F0.wireOp",EDGE,"E26.trimOffspring"),sQuery(id+"F0.wireOp",EDGE,"E27.trimOffspring")])],"isStart":false}),makeQuery(id+"F8.opExtrude","CAP_FACE",FACE,{"disambiguationData":[OSD([subQ0,sQuery(id+"F7.wireOp",EDGE,"E49.top"),sQuery(id+"F7.wireOp",EDGE,"E50.top"),sQuery(id+"F7.wireOp",EDGE,"E50.right"),sQuery(id+"F7.wireOp",EDGE,"E51.top"),sQuery(id+"F7.wireOp",EDGE,"E51.right"),sQuery(id+"F7.wireOp",EDGE,"E52"),sQuery(id+"F7.wireOp",EDGE,"E53")])],"isStart":false})]}),makeQuery(id+"F10.opExtrude","CAP_FACE",FACE,{"disambiguationData":[OSD([subQ2,subQ0,sQuery(id+"F9.wireOp",EDGE,"E54")])],"isStart":true}),makeQuery(id+"F10.opExtrude","CAP_FACE",FACE,{"disambiguationData":[OSD([subQ1,subQ0,sQuery(id+"F9.wireOp",EDGE,"E55")])],"isStart":true})]});}
            var sketch = newSketch(context, id + "F11", { "sketchPlane" : qUnion([Q0])});
            skArc(sketch, "E56", {"start": v(-49.87, 137.02) * mm, "mid": v(-42.45, 126.2) * mm, "end": v(-30, 122.02) * mm});
            skArc(sketch, "E57", {"start": v(10, 122.02) * mm, "mid": v(22.5, 126.2) * mm, "end": v(30, 137.02) * mm});
            skLineSegment(sketch, "E58", {"start": v(-49.87, 137.02) * mm, "end": v(-30, 137.02) * mm});
            skLineSegment(sketch, "E59", {"start": v(-30, 137.02) * mm, "end": v(-30, 122.02) * mm});
            skLineSegment(sketch, "E60", {"start": v(30, 137.02) * mm, "end": v(10, 137.02) * mm});
            skLineSegment(sketch, "E61", {"start": v(10, 137.02) * mm, "end": v(10, 122.02) * mm});
            skSolve(sketch);
        }
        {
            var Q0;
            Q0 = qSketchRegion(id + "F11", true);
            extrude(context, id + "F12", {"entities" : qUnion([Q0]), "operationType" : NewBodyOperationType.REMOVE, "oppositeDirection" : true, "depth" : 12.5 * mm, "offsetDistance" : 25 * mm});
        }
        {
            var Q0;
            Q0=makeQuery(id+"F8.boolean.opBoolean","MERGE",FACE,{"derivedFrom":[makeQuery(id+"F1.opExtrude","CAP_FACE",FACE,{"disambiguationData":[OSD([sQuery(id+"F0.wireOp",EDGE,"E0.top"),sQuery(id+"F0.wireOp",EDGE,"E0.left"),sQuery(id+"F0.wireOp",EDGE,"E0.right"),sQuery(id+"F0.wireOp",EDGE,"E1.bottom"),sQuery(id+"F0.wireOp",EDGE,"E1.top"),sQuery(id+"F0.wireOp",EDGE,"E1.left"),sQuery(id+"F0.wireOp",EDGE,"E1.right"),sQuery(id+"F0.wireOp",EDGE,"E2"),sQuery(id+"F0.wireOp",EDGE,"E5.trimOffspring"),sQuery(id+"F0.wireOp",EDGE,"E6"),sQuery(id+"F0.wireOp",EDGE,"E7"),sQuery(id+"F0.wireOp",EDGE,"E9.trimOffspring"),sQuery(id+"F0.wireOp",EDGE,"E10.bottom"),sQuery(id+"F0.wireOp",EDGE,"E10.top"),sQuery(id+"F0.wireOp",EDGE,"E10.right"),sQuery(id+"F0.wireOp",EDGE,"E11.bottom"),sQuery(id+"F0.wireOp",EDGE,"E11.top"),sQuery(id+"F0.wireOp",EDGE,"E11.right"),sQuery(id+"F0.wireOp",EDGE,"E12.bottom"),sQuery(id+"F0.wireOp",EDGE,"E12.top"),sQuery(id+"F0.wireOp",EDGE,"E12.right"),sQuery(id+"F0.wireOp",EDGE,"E13.bottom"),sQuery(id+"F0.wireOp",EDGE,"E13.top"),sQuery(id+"F0.wireOp",EDGE,"E13.right"),sQuery(id+"F0.wireOp",EDGE,"E14.bottom"),sQuery(id+"F0.wireOp",EDGE,"E14.top"),sQuery(id+"F0.wireOp",EDGE,"E14.right"),sQuery(id+"F0.wireOp",EDGE,"E15.bottom"),sQuery(id+"F0.wireOp",EDGE,"E15.top"),sQuery(id+"F0.wireOp",EDGE,"E15.right"),sQuery(id+"F0.wireOp",EDGE,"E16.bottom"),sQuery(id+"F0.wireOp",EDGE,"E16.top"),sQuery(id+"F0.wireOp",EDGE,"E16.right"),sQuery(id+"F0.wireOp",EDGE,"E17.bottom"),sQuery(id+"F0.wireOp",EDGE,"E17.top"),sQuery(id+"F0.wireOp",EDGE,"E17.right"),sQuery(id+"F0.wireOp",EDGE,"E18.bottom"),sQuery(id+"F0.wireOp",EDGE,"E18.top"),sQuery(id+"F0.wireOp",EDGE,"E18.right"),sQuery(id+"F0.wireOp",EDGE,"E19.trimOffspring"),sQuery(id+"F0.wireOp",EDGE,"E20.trimOffspring"),sQuery(id+"F0.wireOp",EDGE,"E21.trimOffspring"),sQuery(id+"F0.wireOp",EDGE,"E22.trimOffspring"),sQuery(id+"F0.wireOp",EDGE,"E23.trimOffspring"),sQuery(id+"F0.wireOp",EDGE,"E24.trimOffspring"),sQuery(id+"F0.wireOp",EDGE,"E25.trimOffspring"),sQuery(id+"F0.wireOp",EDGE,"E26.trimOffspring"),sQuery(id+"F0.wireOp",EDGE,"E27.trimOffspring")])],"isStart":true}),makeQuery(id+"F8.opExtrude","CAP_FACE",FACE,{"disambiguationData":[OSD([sQuery(id+"F7.wireOp",EDGE,"E49.bottom"),sQuery(id+"F7.wireOp",EDGE,"E49.top"),sQuery(id+"F7.wireOp",EDGE,"E50.top"),sQuery(id+"F7.wireOp",EDGE,"E50.right"),sQuery(id+"F7.wireOp",EDGE,"E51.top"),sQuery(id+"F7.wireOp",EDGE,"E51.right"),sQuery(id+"F7.wireOp",EDGE,"E52"),sQuery(id+"F7.wireOp",EDGE,"E53")])],"isStart":true})]});
            var sketch = newSketch(context, id + "F13", { "sketchPlane" : qUnion([Q0])});
            skLineSegment(sketch, "E62", {"start": v(9.94, 142.02) * mm, "end": v(-5.06, 142.02) * mm});
            skLineSegment(sketch, "E63", {"start": v(9.94, 142.02) * mm, "end": v(24.94, 142.02) * mm});
            skArc(sketch, "E64", {"start": v(-5.06, 142.02) * mm, "mid": v(9.94, 139.72) * mm, "end": v(24.94, 142.02) * mm});
            skSolve(sketch);
        }
        {
            var Q0;
            Q0 = qSketchRegion(id + "F13", true);
            extrude(context, id + "F14", {"entities" : qUnion([Q0]), "operationType" : NewBodyOperationType.REMOVE, "oppositeDirection" : true, "depth" : 30 * mm, "offsetDistance" : 25 * mm});
        }
    });
